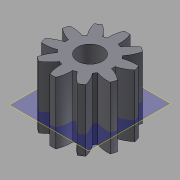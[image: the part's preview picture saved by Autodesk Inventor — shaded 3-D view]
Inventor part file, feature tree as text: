
AUTODESK INVENTOR PART (.ipt)
format: ipt  version: 2015 (Build 190159000, 159)  size: 167,936 bytes
history: native  units: in
note: dims shown in document units (in); Inventor stores cm internally (conversion verified against a paired STEP export)
features: other x13, sketch x3, plane x2
ambient origin geometry x8: Origin, YZ Plane, XZ Plane, XY Plane, X Axis, Y Axis, Z Axis, Center Point
bodies: Solid1 (feature_tree)
feature tree (18):
  other  "Spur Gear1"
  other  "Solid1::Spur Gear1"
  other  "TaggingFeature1"
  sketch  "Sketch1"  dims[d0=0.3937in]
  sketch  "Sketch2"  dims[d16=0.4724in d17=0.0in d41=0.0in d43=0.4724in d46=0.4724in d47=0.0in d48=0.0in]
  sketch  "Sketch3"
  plane  "XZ Plane_1"
  plane  "Work Plane2"
  other  "Z Axis_1"
  other  "Srf1"
  other  "Srf1::Derived"
  other  "Distance iMate"
  other  "Align iMate"
  other  "Mesh iMate"
  other  "Axis iMate"
  other  "Position iMate"
  other  "Mesh iMate2"
  other  "Start plane iMate"
